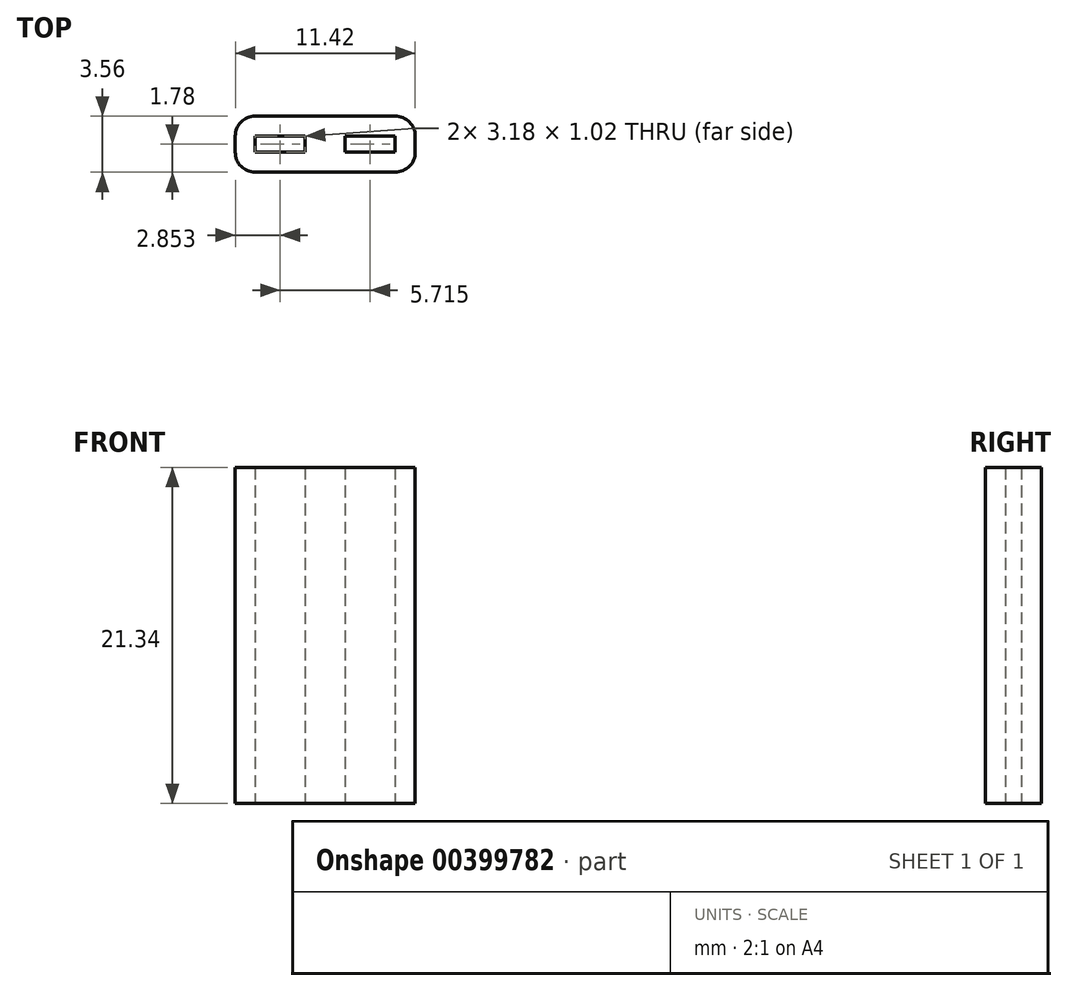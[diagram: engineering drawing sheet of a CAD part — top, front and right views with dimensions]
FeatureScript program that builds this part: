
annotation { "Feature Type Name" : "Feature", "Feature Type Description" : "" }
export const myFeature = defineFeature(function(context is Context, id is Id, definition is map)
    precondition{}
    {
        {
            var Q0;
            Q0=qCreatedBy(makeId("Top.planeOp"),FACE);
            var sketch = newSketch(context, id + "F0", { "sketchPlane" : qUnion([Q0])});
            skLineSegment(sketch, "E0.bottom", {"start": v(-4.45, 0.5) * mm, "end": v(-1.27, 0.5) * mm});
            skLineSegment(sketch, "E0.top", {"start": v(-4.45, -0.5) * mm, "end": v(-1.27, -0.5) * mm});
            skLineSegment(sketch, "E0.left", {"start": v(-4.45, 0.5) * mm, "end": v(-4.45, -0.5) * mm});
            skLineSegment(sketch, "E0.right", {"start": v(4.44, 0.5) * mm, "end": v(4.44, -0.5) * mm});
            skPoint(sketch, "E1", {"position": v(0, 0.5) * mm});
            skPoint(sketch, "E2", {"position": v(-4.45, 0) * mm});
            skLineSegment(sketch, "E3.0", {"start": v(-5.72, 1.78) * mm, "end": v(5.71, 1.78) * mm});
            skLineSegment(sketch, "E3.1", {"start": v(-5.72, 1.78) * mm, "end": v(-5.72, -1.78) * mm});
            skLineSegment(sketch, "E3.2", {"start": v(-5.72, -1.78) * mm, "end": v(5.72, -1.78) * mm});
            skLineSegment(sketch, "E3.3", {"start": v(5.72, 1.78) * mm, "end": v(5.72, -1.78) * mm});
            skLineSegment(sketch, "E4.right", {"start": v(-1.27, 0.5) * mm, "end": v(-1.27, -0.5) * mm});
            skLineSegment(sketch, "E5.MirrorCS", {"start": v(1.27, 0.5) * mm, "end": v(1.27, -0.5) * mm});
            skLineSegment(sketch, "E6.trimOffspring", {"start": v(1.27, 0.5) * mm, "end": v(4.45, 0.5) * mm});
            skPoint(sketch, "E4.left.end.orphan", {"position": v(0, -0.5) * mm});
            skLineSegment(sketch, "E7.trimOffspring", {"start": v(1.27, -0.5) * mm, "end": v(4.45, -0.5) * mm});
            skPoint(sketch, "E8.MirrorCS.end.orphan", {"position": v(1.27, -0.5) * mm});
            skSolve(sketch);
        }
        {
            var Q0;
            Q0=makeQuery(id+"F0.imprint","IMPRINT",FACE,{"disambiguationData":[TD([[makeQuery(id+"F0.imprint","IMPRINT",EDGE,{"derivedFrom":sQuery(id+"F0.wireOp",EDGE,"E0.bottom")}),1.0]])]});
            extrude(context, id + "F1", {"entities" : qUnion([Q0]), "depth" : 21.34 * mm, "offsetDistance" : 25.4 * mm});
        }
        {
            var Q0;
            Q0=makeQuery(id+"F1.opExtrude","SWEPT_EDGE",EDGE,{"disambiguationData":[OSD([sQuery(id+"F0.wireOp",EDGE,"E3.1"),sQuery(id+"F0.wireOp",EDGE,"E3.2")])]});
            var Q1;
            Q1=makeQuery(id+"F1.opExtrude","SWEPT_EDGE",EDGE,{"disambiguationData":[OSD([sQuery(id+"F0.wireOp",EDGE,"E3.0"),sQuery(id+"F0.wireOp",EDGE,"E3.1")])]});
            var Q2;
            Q2=makeQuery(id+"F1.opExtrude","SWEPT_EDGE",EDGE,{"disambiguationData":[OSD([sQuery(id+"F0.wireOp",EDGE,"E3.2"),sQuery(id+"F0.wireOp",EDGE,"E3.3")])]});
            var Q3;
            Q3=makeQuery(id+"F1.opExtrude","SWEPT_EDGE",EDGE,{"disambiguationData":[OSD([sQuery(id+"F0.wireOp",EDGE,"E3.0"),sQuery(id+"F0.wireOp",EDGE,"E3.3")])]});
            fillet(context, id + "F2", {"entities" : qUnion([Q0, Q1, Q2, Q3]), "radius" : 1.27 * mm, "tangentPropagation" : true, "allowEdgeOverflow" : false});
        }
    });
